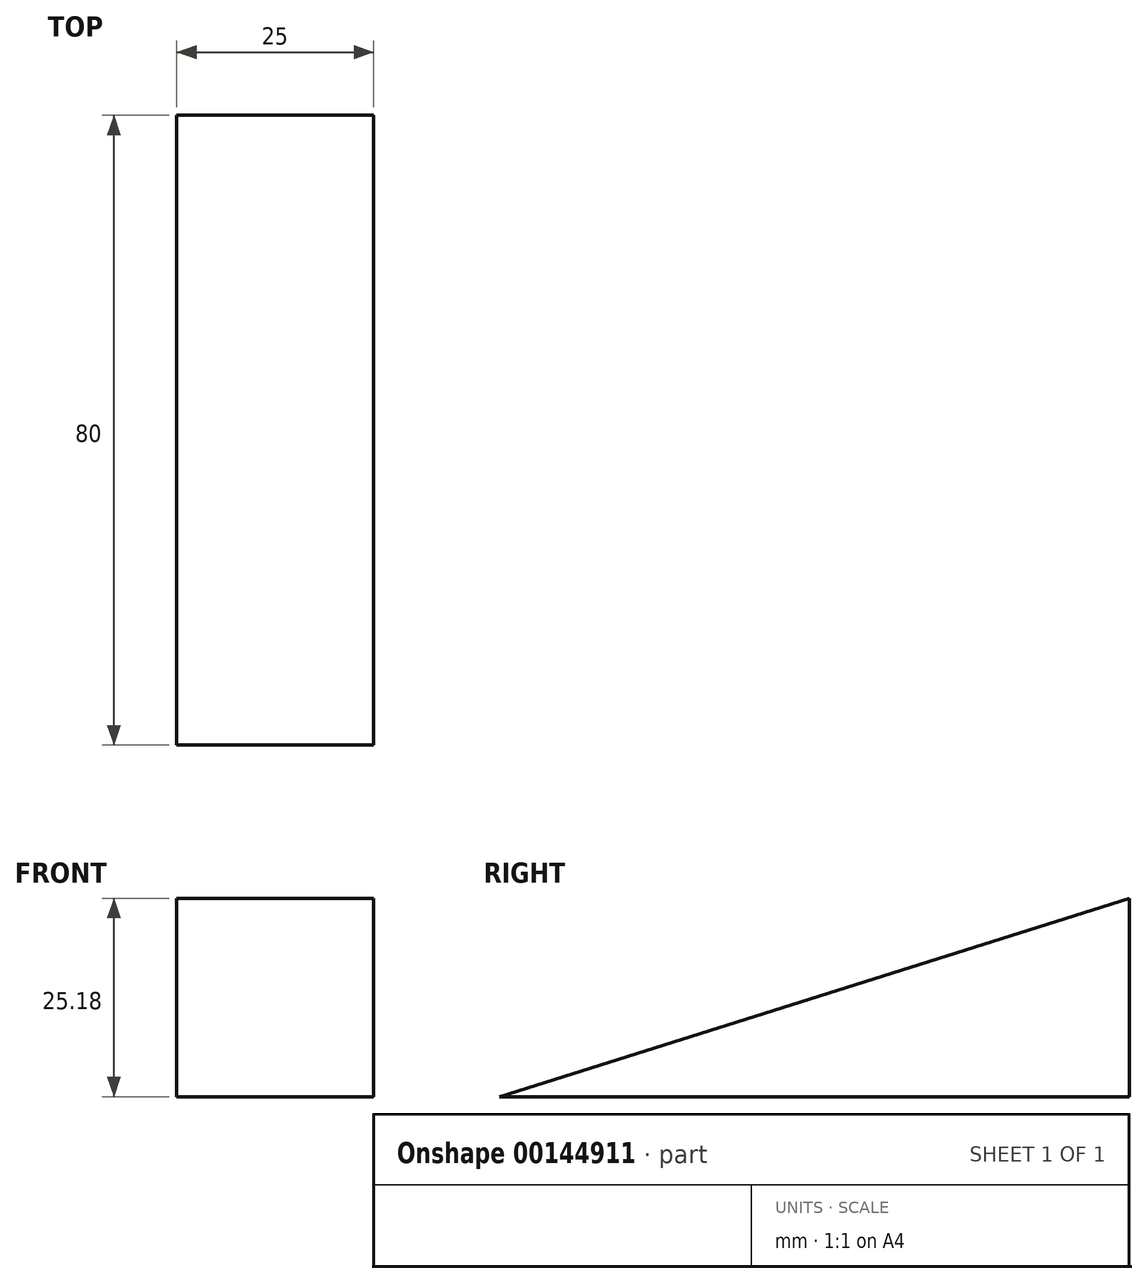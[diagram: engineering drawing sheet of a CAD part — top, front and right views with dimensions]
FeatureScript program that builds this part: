
annotation { "Feature Type Name" : "Feature", "Feature Type Description" : "" }
export const myFeature = defineFeature(function(context is Context, id is Id, definition is map)
    precondition{}
    {
        {
            var Q0;
            Q0=qCreatedBy(makeId("Right.planeOp"),FACE);
            var sketch = newSketch(context, id + "F0", { "sketchPlane" : qUnion([Q0])});
            skLineSegment(sketch, "E0.top", {"start": v(40, -26.54) * mm, "end": v(-40, -26.54) * mm});
            skPoint(sketch, "E0.middle", {"position": v(0, 0) * mm});
            skLineSegment(sketch, "E1", {"start": v(-40, -26.54) * mm, "end": v(40, -1.36) * mm});
            skLineSegment(sketch, "E2", {"start": v(40, -1.36) * mm, "end": v(40, -26.54) * mm});
            skSolve(sketch);
        }
        {
            var Q0;
            Q0 = qSketchRegion(id + "F0", true);
            extrude(context, id + "F1", {"entities" : qUnion([Q0]), "depth" : 25 * mm});
        }
    });
